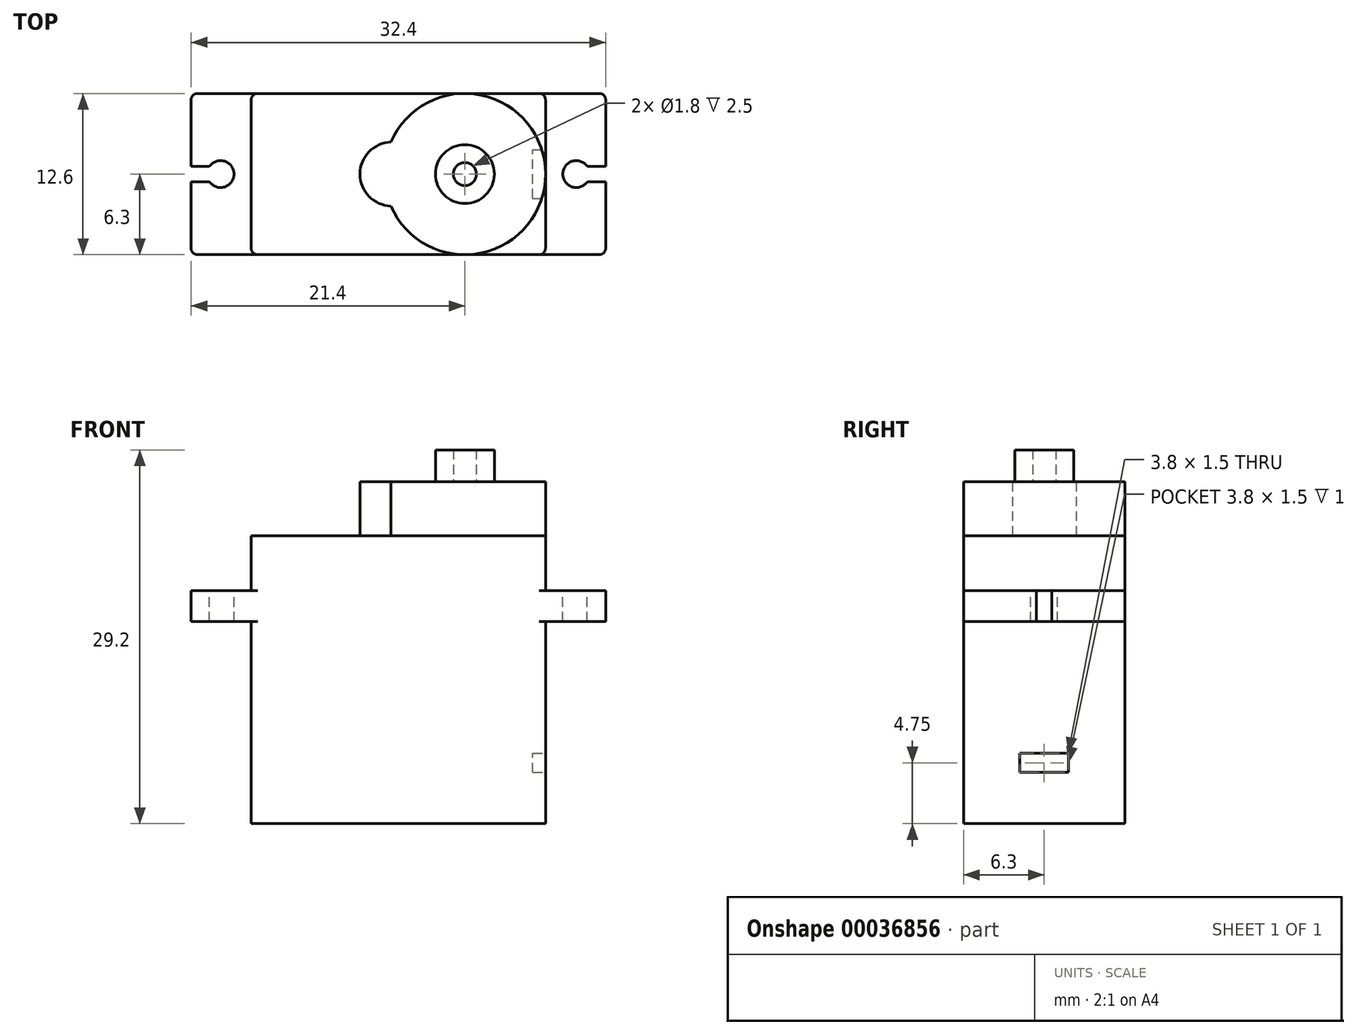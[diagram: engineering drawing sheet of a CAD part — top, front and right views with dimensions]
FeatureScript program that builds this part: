
annotation { "Feature Type Name" : "Feature", "Feature Type Description" : "" }
export const myFeature = defineFeature(function(context is Context, id is Id, definition is map)
    precondition{}
    {
        {
            var Q0;
            Q0=qCreatedBy(makeId("Front.planeOp"),FACE);
            var sketch = newSketch(context, id + "F0", { "sketchPlane" : qUnion([Q0])});
            skLineSegment(sketch, "E0.bottom", {"start": v(0, 0) * mm, "end": v(23, 0) * mm});
            skLineSegment(sketch, "E0.top", {"start": v(0, 22.5) * mm, "end": v(23, 22.5) * mm});
            skLineSegment(sketch, "E0.left", {"start": v(0, 0) * mm, "end": v(0, 22.5) * mm});
            skLineSegment(sketch, "E0.right", {"start": v(23, 0) * mm, "end": v(23, 22.5) * mm});
            skLineSegment(sketch, "E1.bottom", {"start": v(0, 15.8) * mm, "end": v(-4.7, 15.8) * mm});
            skLineSegment(sketch, "E1.top", {"start": v(0, 18.2) * mm, "end": v(-4.7, 18.2) * mm});
            skLineSegment(sketch, "E1.left", {"start": v(0, 15.8) * mm, "end": v(0, 18.2) * mm});
            skLineSegment(sketch, "E1.right", {"start": v(-4.7, 15.8) * mm, "end": v(-4.7, 18.2) * mm});
            skLineSegment(sketch, "E2", {"start": v(11.5, 0) * mm, "end": v(11.5, 38.16) * mm, "construction": true});
            skLineSegment(sketch, "E3.0.MirrorCS", {"start": v(27.7, 15.8) * mm, "end": v(27.7, 18.2) * mm});
            skLineSegment(sketch, "E4.0.MirrorCS", {"start": v(23, 18.2) * mm, "end": v(27.7, 18.2) * mm});
            skLineSegment(sketch, "E5.0.MirrorCS", {"start": v(23, 15.8) * mm, "end": v(27.7, 15.8) * mm});
            skSolve(sketch);
        }
        {
            var Q0;
            Q0=qSketchRegion(id+"F0",true);
            extrude(context, id + "F1", {"entities" : qUnion([Q0]), "depth" : 12.6 * mm});
        }
        {
            var Q0;
            Q0=makeQuery(id+"F1.opExtrude","SWEPT_FACE",FACE,{"disambiguationData":[OSD([sQuery(id+"F0.wireOp",EDGE,"E0.top")])]});
            var sketch = newSketch(context, id + "F2", { "sketchPlane" : qUnion([Q0])});
            skLineSegment(sketch, "E6", {"start": v(23, -6.3) * mm, "end": v(0, -6.3) * mm, "construction": true});
            skArc(sketch, "E7", {"start": v(10.92, -8.8) * mm, "mid": v(23, -6.3) * mm, "end": v(10.92, -3.8) * mm});
            skArc(sketch, "E8", {"start": v(10.92, -3.8) * mm, "mid": v(8.5, -6.3) * mm, "end": v(10.92, -8.8) * mm});
            skSolve(sketch);
        }
        {
            var Q0;
            Q0=qSketchRegion(id+"F2",true);
            extrude(context, id + "F3", {"entities" : qUnion([Q0]), "operationType" : NewBodyOperationType.ADD, "depth" : (26.7 - 22.5) * mm});
        }
        {
            var Q0;
            Q0=makeQuery(id+"F3.opExtrude","CAP_FACE",FACE,{"disambiguationData":[OSD([sQuery(id+"F2.wireOp",EDGE,"E7"),sQuery(id+"F2.wireOp",EDGE,"E8")])],"isStart":false});
            var sketch = newSketch(context, id + "F4", { "sketchPlane" : qUnion([Q0])});
            skCircle(sketch, "E9", {"center": v(16.7, -6.3) * mm, "radius": 0.9 * mm});
            skCircle(sketch, "E10", {"center": v(16.7, -6.3) * mm, "radius": 2.3 * mm});
            skSolve(sketch);
        }
        {
            var Q0;
            Q0=qSketchRegion(id+"F4",true);
            extrude(context, id + "F5", {"entities" : qUnion([Q0]), "operationType" : NewBodyOperationType.ADD, "depth" : (29.2 - 26.7) * mm});
        }
        {
            var Q0;
            Q0=makeQuery(id+"F1.opExtrude","SWEPT_FACE",FACE,{"disambiguationData":[OSD([sQuery(id+"F0.wireOp",EDGE,"E1.top")])]});
            var sketch = newSketch(context, id + "F6", { "sketchPlane" : qUnion([Q0])});
            skLineSegment(sketch, "E11", {"start": v(-4.7, -6.3) * mm, "end": v(30.63, -6.3) * mm, "construction": true});
            skLineSegment(sketch, "E12.0", {"start": v(0, -12.6) * mm, "end": v(23, -12.6) * mm, "construction": true});
            skLineSegment(sketch, "E13.0", {"start": v(0, 0) * mm, "end": v(23, 0) * mm, "construction": true});
            skLineSegment(sketch, "E14", {"start": v(11.5, 0) * mm, "end": v(11.5, -12.6) * mm, "construction": true});
            skArc(sketch, "E15", {"start": v(-3.26, -6.9) * mm, "mid": v(-1.35, -6.3) * mm, "end": v(-3.26, -5.7) * mm});
            skArc(sketch, "E16.0.MirrorC", {"start": v(26.26, -6.9) * mm, "mid": v(24.35, -6.3) * mm, "end": v(26.26, -5.7) * mm});
            skLineSegment(sketch, "E17.bottom", {"start": v(-5.39, -6.9) * mm, "end": v(-3.26, -6.9) * mm});
            skLineSegment(sketch, "E17.top", {"start": v(-5.39, -5.7) * mm, "end": v(-3.26, -5.7) * mm});
            skLineSegment(sketch, "E17.left", {"start": v(-5.39, -6.9) * mm, "end": v(-5.39, -5.7) * mm});
            skLineSegment(sketch, "E18.0.MirrorCS", {"start": v(28.39, -6.9) * mm, "end": v(26.26, -6.9) * mm});
            skLineSegment(sketch, "E18.1.MirrorCS", {"start": v(28.39, -5.7) * mm, "end": v(26.26, -5.7) * mm});
            skLineSegment(sketch, "E18.3.MirrorCS", {"start": v(28.39, -6.9) * mm, "end": v(28.39, -5.7) * mm});
            skSolve(sketch);
        }
        {
            var Q0;
            Q0=qSketchRegion(id+"F6",true);
            extrude(context, id + "F7", {"entities" : qUnion([Q0]), "operationType" : NewBodyOperationType.REMOVE, "oppositeDirection" : true, "depth" : 25 * mm});
        }
        {
            var Q0;
            {var subQ0=sQuery(id+"F0.wireOp",EDGE,"E0.left");Q0=makeQuery(id+"F1.opExtrude","CAP_EDGE",EDGE,{"disambiguationData":[OSD([subQ0]),TDD([makeQuery(id+"F0.imprint","IMPRINT",EDGE,{"disambiguationData":[TD([[makeQuery(id+"F0.imprint","INTERSECT",VERTEX,{"derivedFrom":[sQuery(id+"F0.wireOp",EDGE,"E0.top"),subQ0]}),1.0]])],"derivedFrom":subQ0})])],"isStart":false});}
            var Q1;
            {var subQ0=sQuery(id+"F0.wireOp",EDGE,"E0.left");Q1=makeQuery(id+"F1.opExtrude","CAP_EDGE",EDGE,{"disambiguationData":[OSD([subQ0]),TDD([makeQuery(id+"F0.imprint","IMPRINT",EDGE,{"disambiguationData":[TD([[makeQuery(id+"F0.imprint","INTERSECT",VERTEX,{"derivedFrom":[sQuery(id+"F0.wireOp",EDGE,"E0.bottom"),subQ0]}),-1.0]])],"derivedFrom":subQ0})])],"isStart":false});}
            var Q2;
            {var subQ0=sQuery(id+"F0.wireOp",EDGE,"E0.left");Q2=makeQuery(id+"F1.opExtrude","CAP_EDGE",EDGE,{"disambiguationData":[OSD([subQ0]),TDD([makeQuery(id+"F0.imprint","IMPRINT",EDGE,{"disambiguationData":[TD([[makeQuery(id+"F0.imprint","INTERSECT",VERTEX,{"derivedFrom":[sQuery(id+"F0.wireOp",EDGE,"E0.top"),subQ0]}),1.0]])],"derivedFrom":subQ0})])],"isStart":true});}
            var Q3;
            {var subQ0=sQuery(id+"F0.wireOp",EDGE,"E0.left");Q3=makeQuery(id+"F1.opExtrude","CAP_EDGE",EDGE,{"disambiguationData":[OSD([subQ0]),TDD([makeQuery(id+"F0.imprint","IMPRINT",EDGE,{"disambiguationData":[TD([[makeQuery(id+"F0.imprint","INTERSECT",VERTEX,{"derivedFrom":[sQuery(id+"F0.wireOp",EDGE,"E0.bottom"),subQ0]}),-1.0]])],"derivedFrom":subQ0})])],"isStart":true});}
            var Q4;
            Q4=makeQuery(id+"F1.opExtrude","CAP_EDGE",EDGE,{"disambiguationData":[OSD([sQuery(id+"F0.wireOp",EDGE,"E1.right")])],"isStart":false});
            var Q5;
            Q5=makeQuery(id+"F1.opExtrude","CAP_EDGE",EDGE,{"disambiguationData":[OSD([sQuery(id+"F0.wireOp",EDGE,"E1.right")])],"isStart":true});
            var Q6;
            Q6=makeQuery(id+"F1.opExtrude","CAP_EDGE",EDGE,{"disambiguationData":[OSD([sQuery(id+"F0.wireOp",EDGE,"E3.0.MirrorCS")])],"isStart":false});
            var Q7;
            {var subQ0=sQuery(id+"F0.wireOp",EDGE,"E0.right");Q7=makeQuery(id+"F1.opExtrude","CAP_EDGE",EDGE,{"disambiguationData":[OSD([subQ0]),TDD([makeQuery(id+"F0.imprint","IMPRINT",EDGE,{"disambiguationData":[TD([[makeQuery(id+"F0.imprint","INTERSECT",VERTEX,{"derivedFrom":[sQuery(id+"F0.wireOp",EDGE,"E0.top"),subQ0]}),1.0]])],"derivedFrom":subQ0})])],"isStart":false});}
            var Q8;
            {var subQ0=sQuery(id+"F0.wireOp",EDGE,"E0.right");Q8=makeQuery(id+"F1.opExtrude","CAP_EDGE",EDGE,{"disambiguationData":[OSD([subQ0]),TDD([makeQuery(id+"F0.imprint","IMPRINT",EDGE,{"disambiguationData":[TD([[makeQuery(id+"F0.imprint","INTERSECT",VERTEX,{"derivedFrom":[sQuery(id+"F0.wireOp",EDGE,"E0.bottom"),subQ0]}),-1.0]])],"derivedFrom":subQ0})])],"isStart":false});}
            var Q9;
            Q9=makeQuery(id+"F1.opExtrude","CAP_EDGE",EDGE,{"disambiguationData":[OSD([sQuery(id+"F0.wireOp",EDGE,"E3.0.MirrorCS")])],"isStart":true});
            var Q10;
            {var subQ0=sQuery(id+"F0.wireOp",EDGE,"E0.right");Q10=makeQuery(id+"F1.opExtrude","CAP_EDGE",EDGE,{"disambiguationData":[OSD([subQ0]),TDD([makeQuery(id+"F0.imprint","IMPRINT",EDGE,{"disambiguationData":[TD([[makeQuery(id+"F0.imprint","INTERSECT",VERTEX,{"derivedFrom":[sQuery(id+"F0.wireOp",EDGE,"E0.top"),subQ0]}),1.0]])],"derivedFrom":subQ0})])],"isStart":true});}
            var Q11;
            {var subQ0=sQuery(id+"F0.wireOp",EDGE,"E0.right");Q11=makeQuery(id+"F1.opExtrude","CAP_EDGE",EDGE,{"disambiguationData":[OSD([subQ0]),TDD([makeQuery(id+"F0.imprint","IMPRINT",EDGE,{"disambiguationData":[TD([[makeQuery(id+"F0.imprint","INTERSECT",VERTEX,{"derivedFrom":[sQuery(id+"F0.wireOp",EDGE,"E0.bottom"),subQ0]}),-1.0]])],"derivedFrom":subQ0})])],"isStart":true});}
            fillet(context, id + "F8", {"entities" : qUnion([Q0, Q1, Q2, Q3, Q4, Q5, Q6, Q7, Q8, Q9, Q10, Q11]), "radius" : 0.5 * mm, "tangentPropagation" : true, "allowEdgeOverflow" : false});
        }
        {
            var Q0;
            {var subQ0=sQuery(id+"F0.wireOp",EDGE,"E0.right");Q0=makeQuery(id+"F1.opExtrude","SWEPT_FACE",FACE,{"disambiguationData":[OSD([subQ0]),TDD([makeQuery(id+"F0.imprint","IMPRINT",EDGE,{"disambiguationData":[TD([[makeQuery(id+"F0.imprint","INTERSECT",VERTEX,{"derivedFrom":[sQuery(id+"F0.wireOp",EDGE,"E0.bottom"),subQ0]}),-1.0]])],"derivedFrom":subQ0})])]});}
            var sketch = newSketch(context, id + "F9", { "sketchPlane" : qUnion([Q0])});
            skLineSegment(sketch, "E19.bottom", {"start": v(-8.2, 4) * mm, "end": v(-4.4, 4) * mm});
            skLineSegment(sketch, "E19.top", {"start": v(-8.2, 5.5) * mm, "end": v(-4.4, 5.5) * mm});
            skLineSegment(sketch, "E19.left", {"start": v(-8.2, 4) * mm, "end": v(-8.2, 5.5) * mm});
            skLineSegment(sketch, "E19.right", {"start": v(-4.4, 4) * mm, "end": v(-4.4, 5.5) * mm});
            skLineSegment(sketch, "E20", {"start": v(-6.3, 0) * mm, "end": v(-6.3, 11.49) * mm, "construction": true});
            skSolve(sketch);
        }
        {
            var Q0;
            Q0=qSketchRegion(id+"F9",true);
            extrude(context, id + "F10", {"entities" : qUnion([Q0]), "operationType" : NewBodyOperationType.REMOVE, "oppositeDirection" : true, "depth" : 1 * mm});
        }
        {
            var Q0;
            Q0=makeQuery(id+"F1.opExtrude","SWEPT_BODY",BODY,{"disambiguationData":[OSD([sQuery(id+"F0.wireOp",EDGE,"E0.bottom"),sQuery(id+"F0.wireOp",EDGE,"E0.top"),sQuery(id+"F0.wireOp",EDGE,"E0.left"),sQuery(id+"F0.wireOp",EDGE,"E0.right"),sQuery(id+"F0.wireOp",EDGE,"E1.bottom"),sQuery(id+"F0.wireOp",EDGE,"E1.top"),sQuery(id+"F0.wireOp",EDGE,"E1.right"),sQuery(id+"F0.wireOp",EDGE,"E3.0.MirrorCS"),sQuery(id+"F0.wireOp",EDGE,"E4.0.MirrorCS"),sQuery(id+"F0.wireOp",EDGE,"E5.0.MirrorCS")])]});
            transform(context, id + "F11", {"entities" : qUnion([Q0]), "transformType" : TransformType.TRANSLATION_3D, "dx" : 0 * mm, "dy" : 0 * mm, "dz" : 0 * mm, "makeCopy" : true});
        }
    });
